# Revit family: Cambio Wall Systems - Acoustic - Felt 18x54
name_source: partatom
category: Generic Models
units: mm (PartAtom-declared; Revit-internal decimal feet)

## family parameters
Can host rebar = No
Cut with Voids When Loaded = No
Host = Face
Maintain Annotation Orientation = No
Part Type = Normal
Room Calculation Point = No
Round Connector Dimension = Use Diameter
Shared = No

## types (23) — shared parameters
Default Elevation = 4' - 0"

## per-type parameters (varying)
| type | Cambio Material |
| Felt Color - AZURITE | Cambio Felt - Azurite |
| Felt Color - SLATE | Cambio Felt - Slate |
| Felt Color - SHALE | Cambio Felt - Shale |
| Felt Color - QUARTZ | Cambio Felt - Quartz |
| Felt Color - PERIDOT | Cambio Felt - Peridot |
| Felt Color - OPAL | Cambio Felt - Opal |
| Felt Color - ONYX | Cambio Felt - Onyx |
| Felt Color - NORITE | Cambio Felt - Norite |
| Felt Color - MARL | Cambio Felt - Marl |
| Felt Color - MARBLE | Cambio Felt - Marble |
| Felt Color - JASPER | Cambio Felt - Jasper |
| Felt Color - JADE | Cambio Felt - Jade |
| Felt Color - GRANITE | Cambio Felt - Granite |
| Felt Color - GNEISS | Cambio Felt - Gneiss |
| Felt Color - GABBRO | Cambio Felt - Gabbro |
| Felt Color - FLINT | Cambio Felt - Flint |
| Felt Color - CITRINE | Cambio Felt - Citrine |
| Felt Color - CHALK | Cambio Felt - Chalk |
| Felt Color - AGATE | Cambio Felt - Agate |
| Felt Color - BASALT | Cambio Felt - Basalt |
| Felt Color - SODALITE | Cambio Felt - Sodalite |
| Felt Color - TOURMALINE | Cambio Felt - Tourmaline |
| Felt Color - TUFF | Cambio Felt - Tuff |
